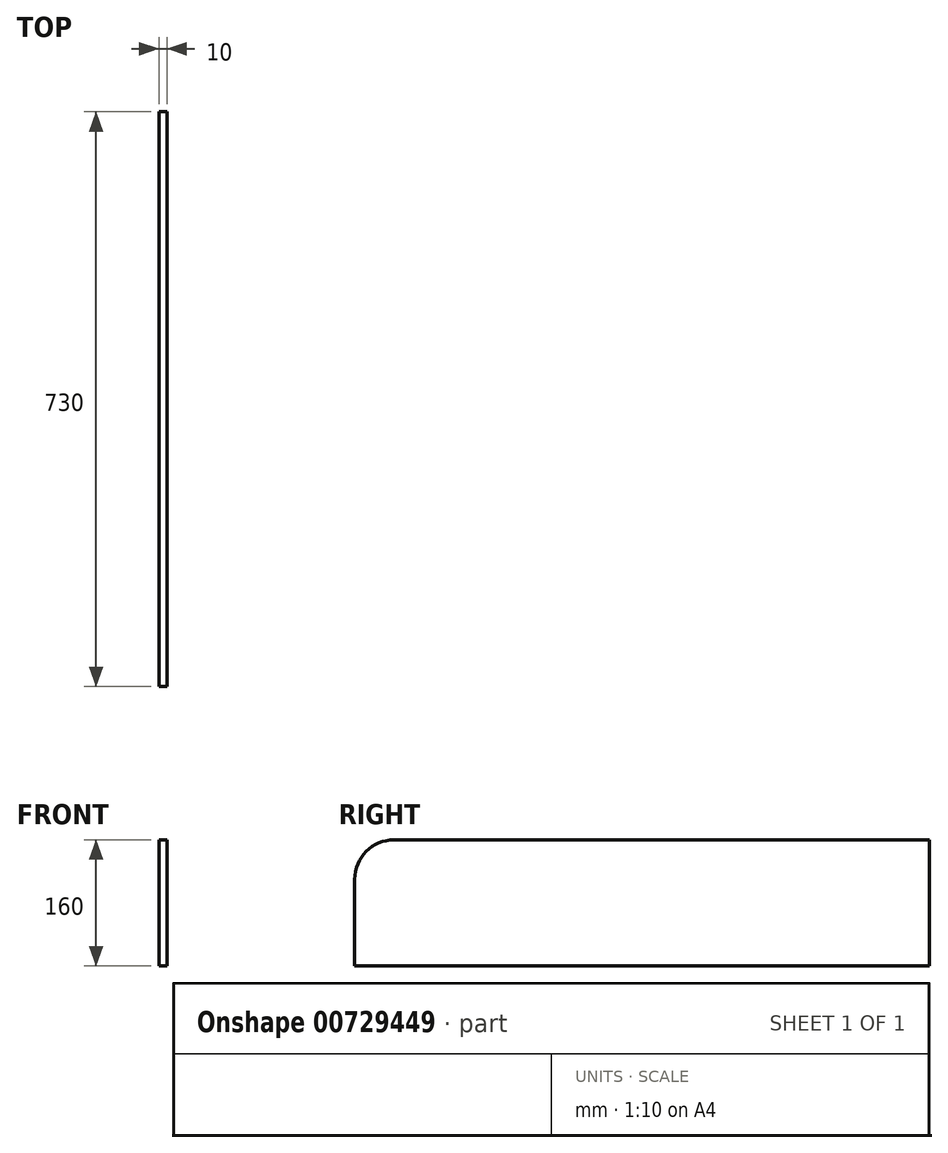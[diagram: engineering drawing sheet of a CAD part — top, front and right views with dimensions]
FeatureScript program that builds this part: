
annotation { "Feature Type Name" : "Feature", "Feature Type Description" : "" }
export const myFeature = defineFeature(function(context is Context, id is Id, definition is map)
    precondition{}
    {
        {
            var Q0;
            Q0=qCreatedBy(makeId("Right.planeOp"),FACE);
            var sketch = newSketch(context, id + "F0", { "sketchPlane" : qUnion([Q0])});
            skLineSegment(sketch, "E0.bottom", {"start": v(-365, -80) * mm, "end": v(365, -80) * mm});
            skLineSegment(sketch, "E0.top", {"start": v(-365, 80) * mm, "end": v(365, 80) * mm});
            skLineSegment(sketch, "E0.left", {"start": v(-365, -80) * mm, "end": v(-365, 80) * mm});
            skLineSegment(sketch, "E0.right", {"start": v(365, -80) * mm, "end": v(365, 80) * mm});
            skPoint(sketch, "E0.middle", {"position": v(0, 0) * mm});
            skSolve(sketch);
        }
        {
            var Q0;
            Q0=makeQuery(id+"F0.imprint","IMPRINT",FACE,{"disambiguationData":[TD([[makeQuery(id+"F0.imprint","IMPRINT",EDGE,{"derivedFrom":sQuery(id+"F0.wireOp",EDGE,"E0.bottom")}),1.0]])]});
            extrude(context, id + "F1", {"entities" : qUnion([Q0]), "depth" : 10 * mm, "offsetDistance" : 25 * mm});
        }
        {
            var Q0;
            Q0=makeQuery(id+"F1.opExtrude","SWEPT_EDGE",EDGE,{"disambiguationData":[OSD([sQuery(id+"F0.wireOp",EDGE,"E0.top"),sQuery(id+"F0.wireOp",EDGE,"E0.left")])]});
            fillet(context, id + "F2", {"entities" : qUnion([Q0]), "radius" : 50 * mm, "tangentPropagation" : true, "allowEdgeOverflow" : false});
        }
    });
